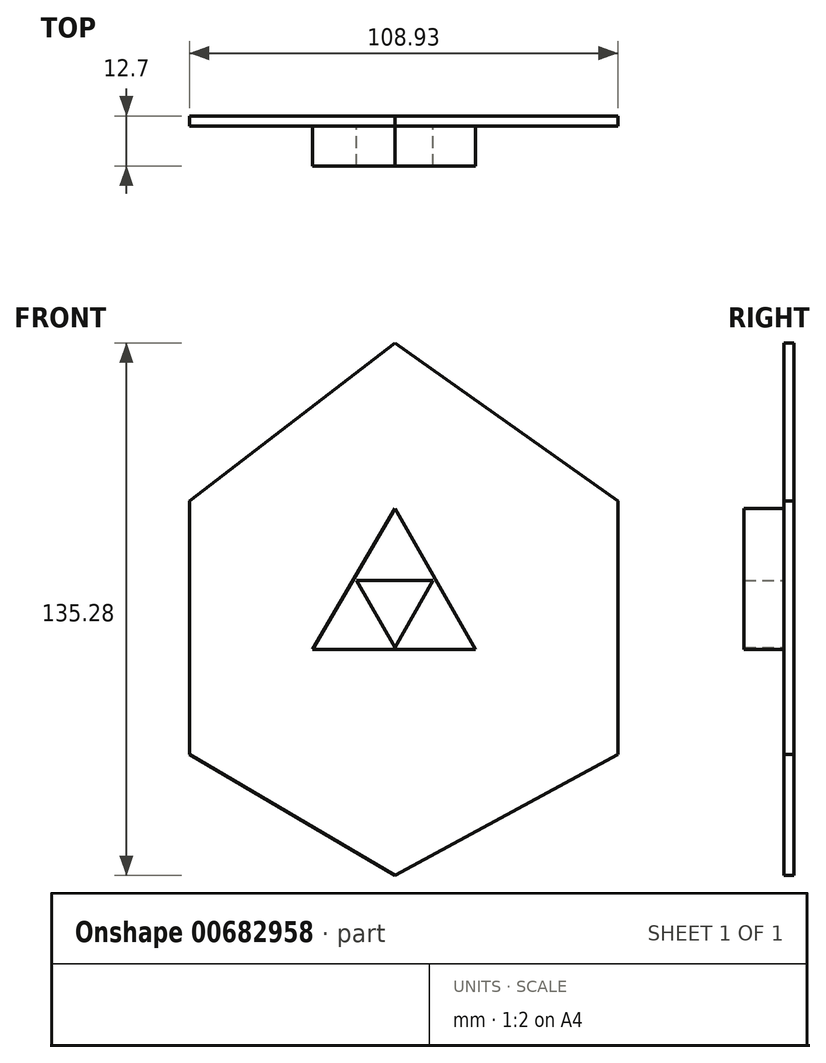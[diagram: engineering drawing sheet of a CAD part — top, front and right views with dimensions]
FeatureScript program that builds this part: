
annotation { "Feature Type Name" : "Feature", "Feature Type Description" : "" }
export const myFeature = defineFeature(function(context is Context, id is Id, definition is map)
    precondition{}
    {
        {
            var Q0;
            Q0=qCreatedBy(makeId("Front.planeOp"),FACE);
            var sketch = newSketch(context, id + "F0", { "sketchPlane" : qUnion([Q0])});
            skLineSegment(sketch, "E0", {"start": v(0, 68.56) * mm, "end": v(59.23, 26.56) * mm});
            skLineSegment(sketch, "E1", {"start": v(59.23, 26.56) * mm, "end": v(59.23, -40.56) * mm});
            skLineSegment(sketch, "E2", {"start": v(59.23, -40.56) * mm, "end": v(0, -72.79) * mm});
            skLineSegment(sketch, "E3", {"start": v(0, -72.79) * mm, "end": v(-54.78, -40.56) * mm});
            skLineSegment(sketch, "E4", {"start": v(-54.78, -40.56) * mm, "end": v(-54.78, 26.56) * mm});
            skLineSegment(sketch, "E5", {"start": v(-54.78, 26.56) * mm, "end": v(0, 68.56) * mm});
            skSolve(sketch);
        }
        {
            var Q0;
            Q0=makeQuery(id+"F0.imprint","IMPRINT",FACE,{"disambiguationData":[TD([[makeQuery(id+"F0.imprint","IMPRINT",EDGE,{"derivedFrom":sQuery(id+"F0.wireOp",EDGE,"E0")}),-1.0]])]});
            extrude(context, id + "F1", {"entities" : qUnion([Q0]), "depth" : 12.7 * mm, "offsetDistance" : 25.4 * mm});
        }
        {
            var Q0;
            Q0=makeQuery(id+"F1.opExtrude","CAP_FACE",FACE,{"disambiguationData":[OSD([sQuery(id+"F0.wireOp",EDGE,"E0"),sQuery(id+"F0.wireOp",EDGE,"E1"),sQuery(id+"F0.wireOp",EDGE,"E2"),sQuery(id+"F0.wireOp",EDGE,"E3"),sQuery(id+"F0.wireOp",EDGE,"E4"),sQuery(id+"F0.wireOp",EDGE,"E5")])],"isStart":false});
            extrude(context, id + "F2", {"entities" : qUnion([Q0]), "operationType" : NewBodyOperationType.REMOVE, "oppositeDirection" : true, "depth" : 2.54 * mm, "offsetDistance" : 25.4 * mm});
        }
        {
            var Q0;
            Q0=makeQuery(id+"F2.boolean.opBoolean","COPY",FACE,{"derivedFrom":makeQuery(id+"F2.opExtrude","CAP_FACE",FACE,{"disambiguationData":[OSD([sQuery(id+"F0.wireOp",EDGE,"E0"),sQuery(id+"F0.wireOp",EDGE,"E1"),sQuery(id+"F0.wireOp",EDGE,"E2"),sQuery(id+"F0.wireOp",EDGE,"E3"),sQuery(id+"F0.wireOp",EDGE,"E4"),sQuery(id+"F0.wireOp",EDGE,"E5")])],"isStart":false})});
            extrude(context, id + "F3", {"entities" : qUnion([Q0]), "operationType" : NewBodyOperationType.REMOVE, "oppositeDirection" : true, "depth" : 7.62 * mm, "offsetDistance" : 25.4 * mm});
        }
        {
            var Q0;
            Q0=makeQuery(id+"F1.opExtrude","SWEPT_FACE",FACE,{"disambiguationData":[OSD([sQuery(id+"F0.wireOp",EDGE,"E0")])]});
            extrude(context, id + "F4", {"entities" : qUnion([Q0]), "operationType" : NewBodyOperationType.REMOVE, "oppositeDirection" : true, "depth" : 2.54 * mm, "offsetDistance" : 25.4 * mm});
        }
        {
            var Q0;
            Q0=makeQuery(id+"F1.opExtrude","SWEPT_FACE",FACE,{"disambiguationData":[OSD([sQuery(id+"F0.wireOp",EDGE,"E5")])]});
            extrude(context, id + "F5", {"entities" : qUnion([Q0]), "operationType" : NewBodyOperationType.REMOVE, "oppositeDirection" : true, "depth" : 2.54 * mm, "offsetDistance" : 25.4 * mm});
        }
        {
            var Q0;
            Q0=makeQuery(id+"F1.opExtrude","SWEPT_FACE",FACE,{"disambiguationData":[OSD([sQuery(id+"F0.wireOp",EDGE,"E1")])]});
            extrude(context, id + "F6", {"entities" : qUnion([Q0]), "operationType" : NewBodyOperationType.REMOVE, "oppositeDirection" : true, "depth" : 2.54 * mm, "offsetDistance" : 25.4 * mm});
        }
        {
            var Q0;
            Q0=makeQuery(id+"F1.opExtrude","SWEPT_FACE",FACE,{"disambiguationData":[OSD([sQuery(id+"F0.wireOp",EDGE,"E4")])]});
            extrude(context, id + "F7", {"entities" : qUnion([Q0]), "operationType" : NewBodyOperationType.REMOVE, "oppositeDirection" : true, "depth" : 2.54 * mm, "offsetDistance" : 25.4 * mm});
        }
        {
            var Q0;
            Q0=makeQuery(id+"F1.opExtrude","SWEPT_FACE",FACE,{"disambiguationData":[OSD([sQuery(id+"F0.wireOp",EDGE,"E3")])]});
            extrude(context, id + "F8", {"entities" : qUnion([Q0]), "operationType" : NewBodyOperationType.REMOVE, "oppositeDirection" : true, "depth" : 2.54 * mm, "offsetDistance" : 25.4 * mm});
        }
        {
            var Q0;
            Q0=makeQuery(id+"F1.opExtrude","SWEPT_FACE",FACE,{"disambiguationData":[OSD([sQuery(id+"F0.wireOp",EDGE,"E2")])]});
            extrude(context, id + "F9", {"entities" : qUnion([Q0]), "operationType" : NewBodyOperationType.REMOVE, "oppositeDirection" : true, "depth" : 2.54 * mm, "offsetDistance" : 25.4 * mm});
        }
        {
            var Q0;
            Q0=makeQuery(id+"F3.boolean.opBoolean","COPY",FACE,{"derivedFrom":makeQuery(id+"F3.opExtrude","CAP_FACE",FACE,{"disambiguationData":[OSD([sQuery(id+"F0.wireOp",EDGE,"E0"),sQuery(id+"F0.wireOp",EDGE,"E1"),sQuery(id+"F0.wireOp",EDGE,"E2"),sQuery(id+"F0.wireOp",EDGE,"E3"),sQuery(id+"F0.wireOp",EDGE,"E4"),sQuery(id+"F0.wireOp",EDGE,"E5")])],"isStart":false})});
            var sketch = newSketch(context, id + "F10", { "sketchPlane" : qUnion([Q0])});
            skLineSegment(sketch, "E6", {"start": v(-20.9, -12.43) * mm, "end": v(0, 23.38) * mm});
            skLineSegment(sketch, "E7", {"start": v(0, 23.38) * mm, "end": v(20.43, -12.37) * mm});
            skLineSegment(sketch, "E8", {"start": v(20.43, -12.37) * mm, "end": v(-20.9, -12.43) * mm});
            skLineSegment(sketch, "E9", {"start": v(-9.82, 5.07) * mm, "end": v(9.7, 5.1) * mm});
            skLineSegment(sketch, "E10", {"start": v(9.7, 5.1) * mm, "end": v(-0.06, -11.88) * mm});
            skLineSegment(sketch, "E11", {"start": v(-0.06, -11.88) * mm, "end": v(-9.82, 5.07) * mm});
            skSolve(sketch);
        }
        {
            var Q0;
            Q0=makeQuery(id+"F10.imprint","IMPRINT",FACE,{"disambiguationData":[TD([[makeQuery(id+"F10.imprint","IMPRINT",EDGE,{"derivedFrom":sQuery(id+"F10.wireOp",EDGE,"E6")}),-1.0]])]});
            extrude(context, id + "F11", {"entities" : qUnion([Q0]), "operationType" : NewBodyOperationType.ADD, "depth" : 10.16 * mm, "offsetDistance" : 25.4 * mm});
        }
    });
